# Revit family: TV-016_RFA
name_source: partatom
category: Aparatos sanitarios
units: mm (PartAtom-declared; Revit-internal decimal feet)

## family parameters
Activar corte en vistas = No
Anfitrión = Cara
Compartido = Sí
Corte con vacíos al cargar = No
Cota de conector redondo = Usar diámetro
Mantener orientación de anotación = No
Número OmniClass = 23.45.00.00
Punto de cálculo de habitación = Sí
Tipo de pieza = Normal
Título OmniClass = Sanitary, Laundry, and Cleaning Equipment

## types (1)
- TV-016
    Brass Chromed = Brass
    Comentarios de tipo = Céspol para lavabo
    Descripción = Céspol para lavabo con registro. No incluye contra. Acabado cromo
    Elevación por defecto = 1.25"
    Fabricante = HELVEX S.A DE C.V
    Imagen de tipo = TV-016.jpg
    Inlet Threads = Ø1¼" (32mm) Pipe
    Modelo = TV-016
    Support Base Diameter = 2.70"
    Total Height = 9.70"
    Total Length = 5.20"
    URL = https://helvex.com.mx

## geometry (parser evidence)
native form markers: Blend x4, Sweep x5
no freeform markers — native parametric forms only
